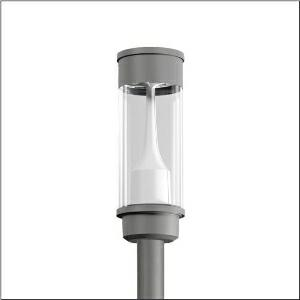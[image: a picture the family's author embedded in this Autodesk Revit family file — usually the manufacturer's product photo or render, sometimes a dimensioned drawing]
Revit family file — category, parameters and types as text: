
# Revit family: litepole_iq___pl1_2s_5xa5415cf14h_d917
name_source: partatom
category: Lighting Fixtures
units: mm (PartAtom-declared; Revit-internal decimal feet)

## family parameters
Cut with Voids When Loaded = No
Host = Face
Light Source = No
Part Type = Normal
Room Calculation Point = No
Round Connector Dimension = Use Diameter
Shared = No

## types (1)
- --- (1 x LED, 2970 lm, 23.9 W, 2200K)
    Apparent Load = 24 VA
    CIE Flux Codes = 23 62 94 96 100
    Color Rendering = 70
    Color Temperature = 2200K
    Default Elevation = 1800 mm
    Description = Litepole iQ, mast luminaire, Module 540 iQ-SR, primary light control with 3 zone facetted reflector, of plastic, silver coated, highly specular, structured, primary optical cover: cover, of PMMA, transparent, partly coated, light distribution: PL1.2s, light emission: direct distribution, primary light characteristic: symmetric, installation type: post-top, LED, High Power LED, rated luminous flux: 2.970lm, luminous efficacy: 124lm/W, light colour: 722, colour temperature: 2200K, control gear: iQ Street-Remote, control: optimised constant luminous flux control (CLO 2.0), Desk-Remote (wireless, voltage-free reading and setting of iQ features in the workshop via application-optimized NFC function/RFID function), Light-Fading, Smart-Wire, Night-Set, Lumen-Switch, Temp-Guard, Auto-Match, Street-Remote, pre-setting: logarithmic dimming characteristic, with terminal, 6-pole, max. 2.5mm², mains connection: 230..240V, AC, 50/60Hz, start of lifetime: 24W, end of service life: 26W, reduction: 12W, luminaire housing, upper part, of glass-fibre reinforced polyester, coated, Siteco® metallic grey (DB 702S), diameter: 210mm, height: 590mm, spigot size: d x l = 76 x 70mm (post-top) | with reducer (optional accessory) 60 x 70mm, mounting height: 3..5m, post-top mast mounting element, of diecast aluminium, coated, Siteco® metallic grey (DB 702S), Module 540 iQ-SR, traffic white (RAL 9016), equipment: standard, protection rating (complete): IP65, insulation class (complete): insulation class II (safety insulation), certification: CE, ENEC, VDE, packaging unit: 1 piece

Light Distribution: PL1.2s
    Height = 590 mm
    Lamp = 1 x LED
    Lamp Light Flux = 2970 lm
    Lamp Power = 23.9 W
    Lamp count = 1
    Length = 220 mm
    Luminous efficacy = 124 lm/W
    Manufacturer = Siteco
    ModVariant = No
    Model = 5XA5415CF14H
    Number of Poles = 1
    OnlyDefault = Yes
    Power Factor = 1
    Product Name = Litepole iQ | PL1.2s
    Product group = mast luminaire | pylon top
    ProductGroupID = 6100
    Protection Class = Protection class II
    Protection Degree = IP 65
    RLX_Detail_Level = 1
    RLX_Emergency_Light_Flux = 0 lm
    RLX_Emergency_Type = 0
    RLX_Emergency_Type_DB = No
    RlxData = <blob elided: 40233 chars, md5=0d0afcdf>
    Socket = socket
    Standby Power = 0 W
    System Light Flux = 2970 lm
    System Power = 24 W
    Type Comments = factory setting: luminous flux: 100 % | dim-lin: 254 | 499 mA
    Type Image = l_1006025.jpg
    URL = http://relux.com
    VarID = @adj_144359
    Voltage = 0 V
    Weight = 0.00 kg
    Width = 0 mm  [stored 0 ft]

note: [stored X ft] marks values corroborated as IEEE doubles in the binary element streams (Revit-internal decimal feet)

## geometry (parser evidence)
native form markers: Blend x4, Sweep x9
no freeform markers — native parametric forms only
